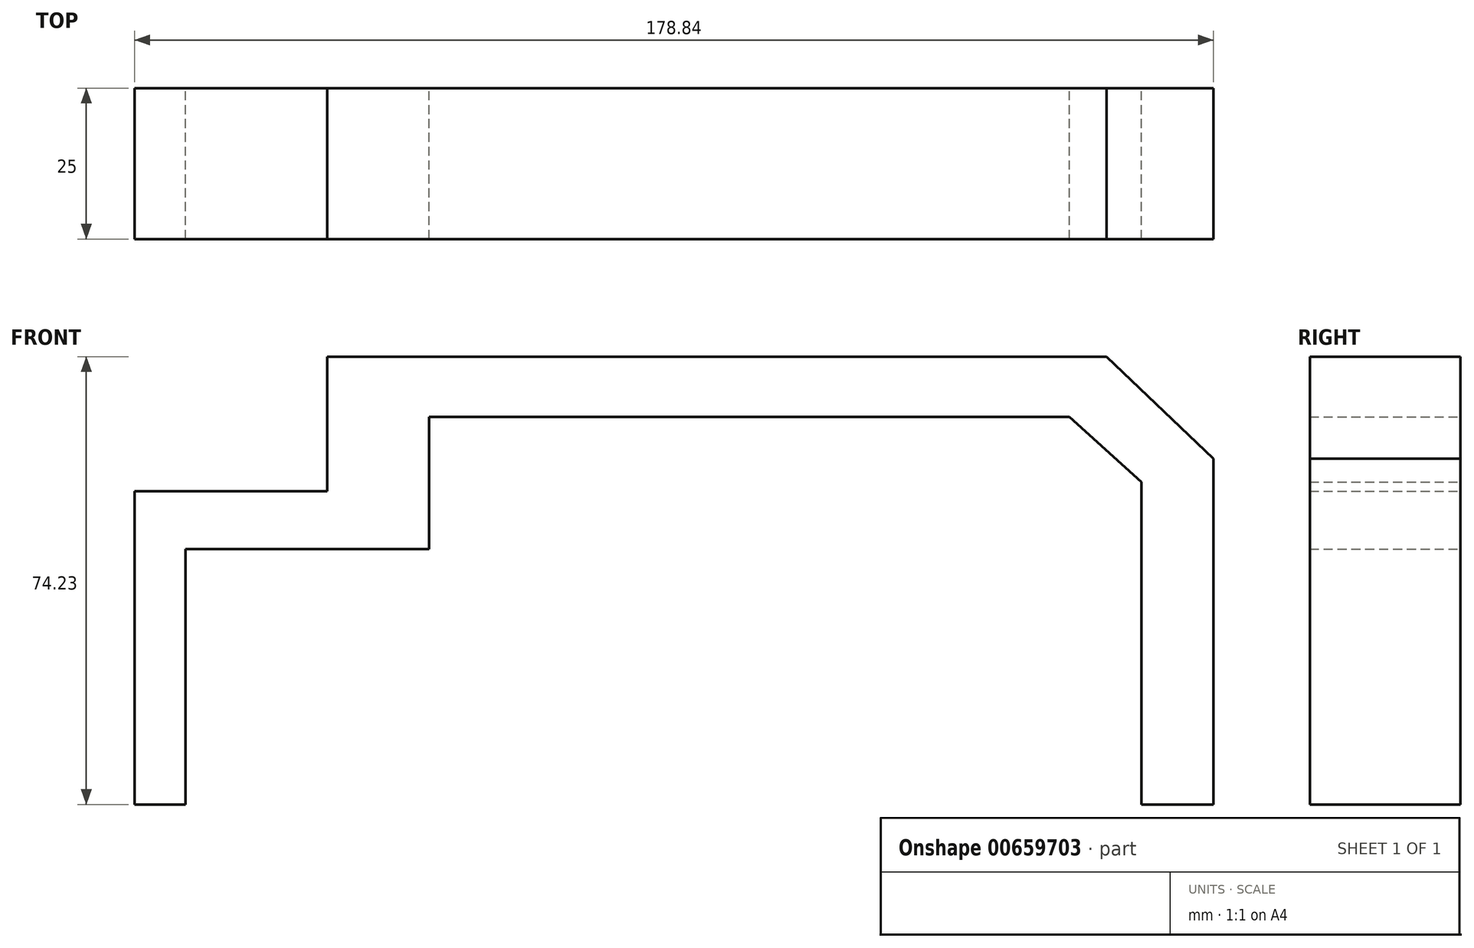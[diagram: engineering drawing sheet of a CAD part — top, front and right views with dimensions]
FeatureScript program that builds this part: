
annotation { "Feature Type Name" : "Feature", "Feature Type Description" : "" }
export const myFeature = defineFeature(function(context is Context, id is Id, definition is map)
    precondition{}
    {
        {
            var Q0;
            Q0=qCreatedBy(makeId("Front.planeOp"),FACE);
            var sketch = newSketch(context, id + "F0", { "sketchPlane" : qUnion([Q0])});
            skLineSegment(sketch, "E0", {"start": v(-119.42, 0) * mm, "end": v(-119.42, 51.92) * mm});
            skLineSegment(sketch, "E1", {"start": v(-119.42, 51.92) * mm, "end": v(-87.5, 51.92) * mm});
            skLineSegment(sketch, "E2", {"start": v(-87.5, 51.92) * mm, "end": v(-87.5, 74.23) * mm});
            skLineSegment(sketch, "E3", {"start": v(-87.5, 74.23) * mm, "end": v(41.73, 74.23) * mm});
            skLineSegment(sketch, "E4", {"start": v(41.73, 74.23) * mm, "end": v(59.42, 57.3) * mm});
            skLineSegment(sketch, "E5", {"start": v(59.42, 57.3) * mm, "end": v(59.42, 0) * mm});
            skLineSegment(sketch, "E6", {"start": v(59.42, 0) * mm, "end": v(47.5, 0) * mm});
            skLineSegment(sketch, "E7", {"start": v(47.5, 0) * mm, "end": v(47.5, 53.46) * mm});
            skLineSegment(sketch, "E8", {"start": v(47.5, 53.46) * mm, "end": v(35.58, 64.23) * mm});
            skLineSegment(sketch, "E9", {"start": v(35.58, 64.23) * mm, "end": v(-70.58, 64.23) * mm});
            skLineSegment(sketch, "E10", {"start": v(-70.58, 64.23) * mm, "end": v(-70.58, 42.3) * mm});
            skLineSegment(sketch, "E11", {"start": v(-70.58, 42.3) * mm, "end": v(-110.96, 42.3) * mm});
            skLineSegment(sketch, "E12", {"start": v(-110.96, 42.3) * mm, "end": v(-110.96, 0) * mm});
            skLineSegment(sketch, "E13", {"start": v(-110.96, 0) * mm, "end": v(-119.42, 0) * mm});
            skSolve(sketch);
        }
        {
            var Q0;
            Q0=makeQuery(id+"F0.imprint","IMPRINT",FACE,{"disambiguationData":[TD([[makeQuery(id+"F0.imprint","IMPRINT",EDGE,{"derivedFrom":sQuery(id+"F0.wireOp",EDGE,"E0")}),-1.0]])]});
            extrude(context, id + "F1", {"entities" : qUnion([Q0]), "depth" : 25 * mm, "offsetDistance" : 25 * mm});
        }
    });
